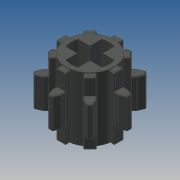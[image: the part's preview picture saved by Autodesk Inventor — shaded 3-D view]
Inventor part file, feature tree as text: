
AUTODESK INVENTOR PART (.ipt)
format: ipt  version: 2022.2 (Build 262287000, 287)  size: 616,960 bytes
history: native  units: in
note: dims shown in document units (in); Inventor stores cm internally (conversion verified against a paired STEP export)
features: extrude x3, sketch x2, fillet x2, mirror x1, pattern_circular x1
ambient origin geometry x8: Origin, YZ Plane, XZ Plane, XY Plane, X Axis, Y Axis, Z Axis, Center Point
bodies: Solid1 (feature_tree)
feature tree (9):
  sketch  "Sketch2"  dims[d0=0.189in d1=0.2362in]
  extrude  "Extrusion1"  Depth=0.2362in
  extrude  "Extrusion2"  Depth=0.0039in
  extrude  "Extrusion3"  TaperAngle=0.0deg  [1 undecoded]
  mirror  "Mirror1"
  fillet  "Fillet1"  Radius=0.0631in
  pattern_circular  "Circular Pattern1"  [2 undecoded]
  fillet  "Fillet2"  Radius=0.0776in
  sketch  "Sketch3"  dims[d2=0.063in d3=0.315in d4=0.0in d5=0.0631in d6=0.022in d8=0.0776in d9=0.0425in d10=0.0472in d11=0.2956in d12=0.3087in d13=0.0in d14=0.0039in d15=3.1496in d16=360.0deg d18=0.0039in d19=0.0795in d20=0.0in d21=0.0524in d22=0.0in d23=0.0in d24=0.0in]
note: 3 required parameter values undecoded (feature->parameter linkage not recoverable at this tier; creation-order binding heuristic only, values carry confidence <= 0.55)
